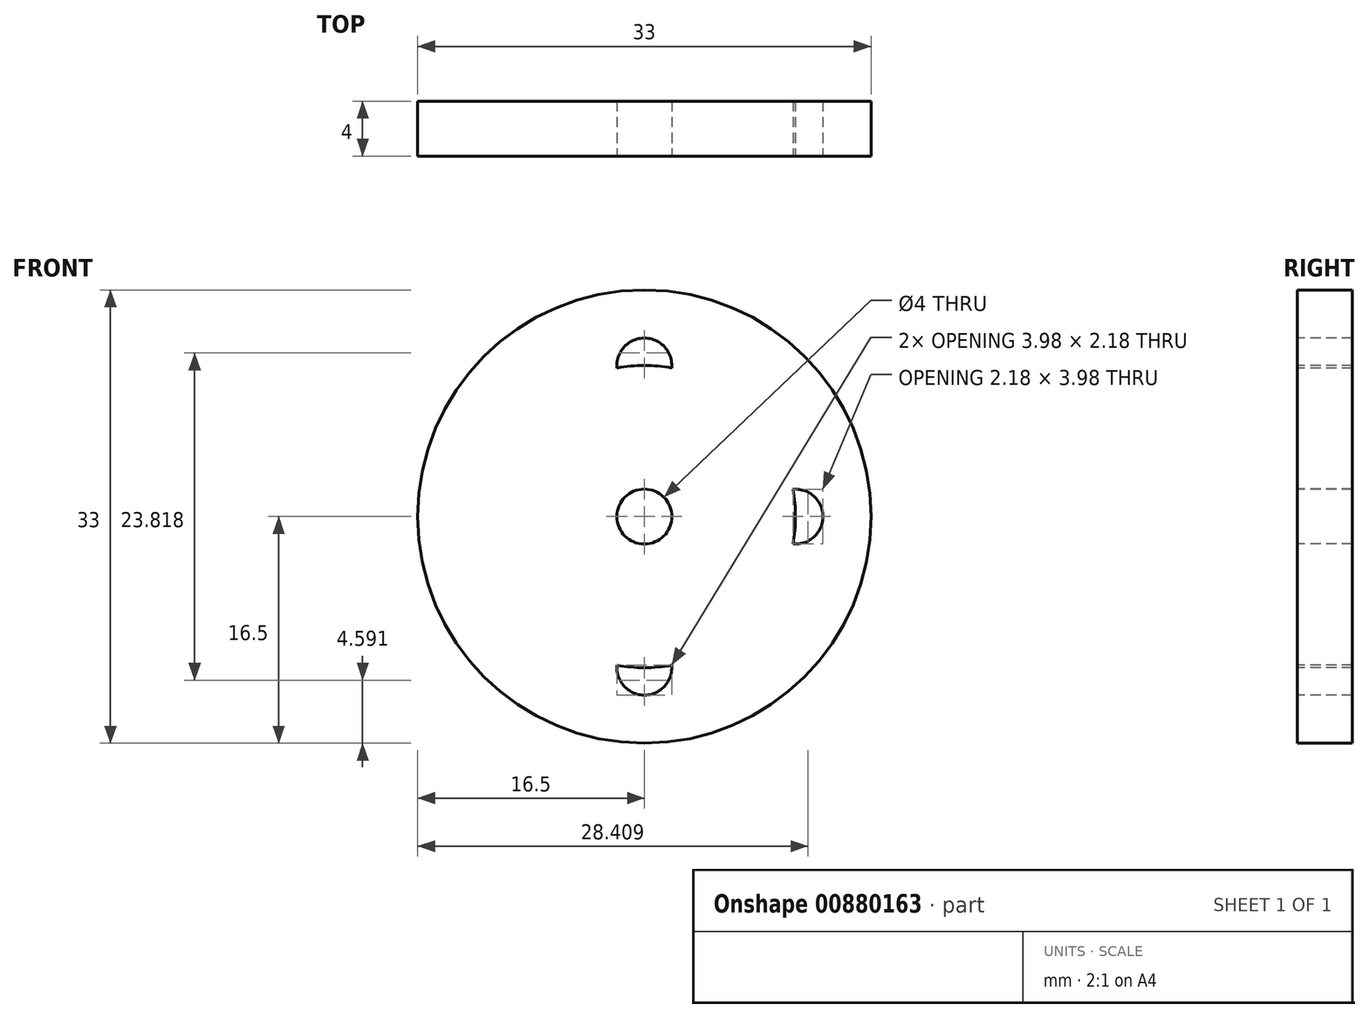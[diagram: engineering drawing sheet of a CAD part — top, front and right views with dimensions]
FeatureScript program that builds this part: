
annotation { "Feature Type Name" : "Feature", "Feature Type Description" : "" }
export const myFeature = defineFeature(function(context is Context, id is Id, definition is map)
    precondition{}
    {
        {
            var Q0;
            Q0=qCreatedBy(makeId("Front.planeOp"),FACE);
            var sketch = newSketch(context, id + "F0", { "sketchPlane" : qUnion([Q0])});
            skCircle(sketch, "E0", {"center": v(0, 0) * mm, "radius": 16.5 * mm});
            skSolve(sketch);
        }
        {
            var Q0;
            Q0 = qSketchRegion(id + "F0", true);
            extrude(context, id + "F1", {"entities" : qUnion([Q0]), "depth" : 4 * mm, "offsetDistance" : 25 * mm});
        }
        {
            var Q0;
            Q0=makeQuery(id+"F1.opExtrude","CAP_FACE",FACE,{"disambiguationData":[OSD([sQuery(id+"F0.wireOp",EDGE,"E0")])],"isStart":false});
            var sketch = newSketch(context, id + "F2", { "sketchPlane" : qUnion([Q0])});
            skLineSegment(sketch, "E1", {"start": v(0, 0) * mm, "end": v(-16.5, 0) * mm});
            skLineSegment(sketch, "E2", {"start": v(-16.5, 0) * mm, "end": v(0, 0) * mm});
            skLineSegment(sketch, "E3", {"start": v(0, 0) * mm, "end": v(0, 16.5) * mm});
            skLineSegment(sketch, "E4", {"start": v(0, 0) * mm, "end": v(0, -16.5) * mm});
            skLineSegment(sketch, "E5", {"start": v(0, 0) * mm, "end": v(16.5, 0) * mm});
            skLineSegment(sketch, "E6", {"start": v(16.5, 0) * mm, "end": v(9.5, 0) * mm});
            skLineSegment(sketch, "E7", {"start": v(-16.5, 0) * mm, "end": v(-9.5, 0) * mm});
            skLineSegment(sketch, "E8", {"start": v(0, -16.5) * mm, "end": v(0, -9.5) * mm});
            skLineSegment(sketch, "E9", {"start": v(0, 16.5) * mm, "end": v(0, 9.5) * mm});
            skCircle(sketch, "E10", {"center": v(0, 0) * mm, "radius": 2 * mm});
            skCircle(sketch, "E11", {"center": v(0, 0) * mm, "radius": 11 * mm});
            skCircle(sketch, "E12", {"center": v(0, 11) * mm, "radius": 2 * mm});
            skCircle(sketch, "E13", {"center": v(11, 0) * mm, "radius": 2 * mm});
            skCircle(sketch, "E14", {"center": v(0, -11) * mm, "radius": 2 * mm});
            skCircle(sketch, "E15", {"center": v(-11, 0) * mm, "radius": 2 * mm});
            skSolve(sketch);
        }
        {
            var Q0;
            {var subQ0=sQuery(id+"F2.wireOp",EDGE,"E7");var subQ1=sQuery(id+"F2.wireOp",EDGE,"E2");var subQ2=makeQuery(id+"F2.imprint","INTERSECT",VERTEX,{"derivedFrom":[subQ1,subQ0]});Q0=makeQuery(id+"F2.imprint","IMPRINT",FACE,{"disambiguationData":[TD([[makeQuery(id+"F2.imprint","IMPRINT",EDGE,{"disambiguationData":[TD([[subQ2,-1.0]])],"derivedFrom":subQ1}),1.0]])]});}
            var Q1;
            {var subQ0=sQuery(id+"F2.wireOp",EDGE,"E7");var subQ1=sQuery(id+"F2.wireOp",EDGE,"E2");var subQ2=makeQuery(id+"F2.imprint","INTERSECT",VERTEX,{"derivedFrom":[subQ1,subQ0]});Q1=makeQuery(id+"F2.imprint","IMPRINT",FACE,{"disambiguationData":[TD([[makeQuery(id+"F2.imprint","IMPRINT",EDGE,{"disambiguationData":[TD([[subQ2,-1.0]])],"derivedFrom":subQ1}),-1.0]])]});}
            var Q2;
            {var subQ0=sQuery(id+"F2.wireOp",EDGE,"E9");var subQ1=sQuery(id+"F2.wireOp",EDGE,"E3");var subQ2=makeQuery(id+"F2.imprint","INTERSECT",VERTEX,{"derivedFrom":[subQ1,subQ0]});Q2=makeQuery(id+"F2.imprint","IMPRINT",FACE,{"disambiguationData":[TD([[makeQuery(id+"F2.imprint","IMPRINT",EDGE,{"disambiguationData":[TD([[subQ2,1.0]])],"derivedFrom":subQ1}),-1.0]])]});}
            var Q3;
            {var subQ0=sQuery(id+"F2.wireOp",EDGE,"E9");var subQ1=sQuery(id+"F2.wireOp",EDGE,"E3");var subQ2=makeQuery(id+"F2.imprint","INTERSECT",VERTEX,{"derivedFrom":[subQ1,subQ0]});Q3=makeQuery(id+"F2.imprint","IMPRINT",FACE,{"disambiguationData":[TD([[makeQuery(id+"F2.imprint","IMPRINT",EDGE,{"disambiguationData":[TD([[subQ2,1.0]])],"derivedFrom":subQ1}),1.0]])]});}
            var Q4;
            {var subQ0=sQuery(id+"F2.wireOp",EDGE,"E8");var subQ1=sQuery(id+"F2.wireOp",EDGE,"E4");var subQ2=makeQuery(id+"F2.imprint","INTERSECT",VERTEX,{"derivedFrom":[subQ1,subQ0]});Q4=makeQuery(id+"F2.imprint","IMPRINT",FACE,{"disambiguationData":[TD([[makeQuery(id+"F2.imprint","IMPRINT",EDGE,{"disambiguationData":[TD([[subQ2,1.0]])],"derivedFrom":subQ1}),-1.0]])]});}
            var Q5;
            {var subQ0=sQuery(id+"F2.wireOp",EDGE,"E8");var subQ1=sQuery(id+"F2.wireOp",EDGE,"E4");var subQ2=makeQuery(id+"F2.imprint","INTERSECT",VERTEX,{"derivedFrom":[subQ1,subQ0]});Q5=makeQuery(id+"F2.imprint","IMPRINT",FACE,{"disambiguationData":[TD([[makeQuery(id+"F2.imprint","IMPRINT",EDGE,{"disambiguationData":[TD([[subQ2,1.0]])],"derivedFrom":subQ1}),1.0]])]});}
            var Q6;
            {var subQ0=sQuery(id+"F2.wireOp",EDGE,"E6");var subQ1=sQuery(id+"F2.wireOp",EDGE,"E5");var subQ2=makeQuery(id+"F2.imprint","INTERSECT",VERTEX,{"derivedFrom":[subQ1,subQ0]});Q6=makeQuery(id+"F2.imprint","IMPRINT",FACE,{"disambiguationData":[TD([[makeQuery(id+"F2.imprint","IMPRINT",EDGE,{"disambiguationData":[TD([[subQ2,1.0]])],"derivedFrom":subQ1}),1.0]])]});}
            var Q7;
            {var subQ0=sQuery(id+"F2.wireOp",EDGE,"E6");var subQ1=sQuery(id+"F2.wireOp",EDGE,"E5");var subQ2=makeQuery(id+"F2.imprint","INTERSECT",VERTEX,{"derivedFrom":[subQ1,subQ0]});Q7=makeQuery(id+"F2.imprint","IMPRINT",FACE,{"disambiguationData":[TD([[makeQuery(id+"F2.imprint","IMPRINT",EDGE,{"disambiguationData":[TD([[subQ2,1.0]])],"derivedFrom":subQ1}),-1.0]])]});}
            var Q8;
            {var subQ0=sQuery(id+"F2.wireOp",EDGE,"E13");var subQ1=sQuery(id+"F2.wireOp",EDGE,"E6");var subQ2=makeQuery(id+"F2.imprint","INTERSECT",VERTEX,{"derivedFrom":[subQ1,subQ0]});Q8=makeQuery(id+"F2.imprint","IMPRINT",FACE,{"disambiguationData":[TD([[makeQuery(id+"F2.imprint","IMPRINT",EDGE,{"disambiguationData":[TD([[subQ2,-1.0]])],"derivedFrom":subQ1}),-1.0]])]});}
            var Q9;
            {var subQ0=sQuery(id+"F2.wireOp",EDGE,"E13");var subQ1=sQuery(id+"F2.wireOp",EDGE,"E6");var subQ2=makeQuery(id+"F2.imprint","INTERSECT",VERTEX,{"derivedFrom":[subQ1,subQ0]});Q9=makeQuery(id+"F2.imprint","IMPRINT",FACE,{"disambiguationData":[TD([[makeQuery(id+"F2.imprint","IMPRINT",EDGE,{"disambiguationData":[TD([[subQ2,-1.0]])],"derivedFrom":subQ1}),1.0]])]});}
            var Q10;
            {var subQ0=sQuery(id+"F2.wireOp",EDGE,"E15");var subQ1=sQuery(id+"F2.wireOp",EDGE,"E7");var subQ2=makeQuery(id+"F2.imprint","INTERSECT",VERTEX,{"derivedFrom":[subQ1,subQ0]});Q10=makeQuery(id+"F2.imprint","IMPRINT",FACE,{"disambiguationData":[TD([[makeQuery(id+"F2.imprint","IMPRINT",EDGE,{"disambiguationData":[TD([[subQ2,-1.0]])],"derivedFrom":subQ1}),1.0]])]});}
            var Q11;
            {var subQ0=sQuery(id+"F2.wireOp",EDGE,"E15");var subQ1=sQuery(id+"F2.wireOp",EDGE,"E7");var subQ2=makeQuery(id+"F2.imprint","INTERSECT",VERTEX,{"derivedFrom":[subQ1,subQ0]});Q11=makeQuery(id+"F2.imprint","IMPRINT",FACE,{"disambiguationData":[TD([[makeQuery(id+"F2.imprint","IMPRINT",EDGE,{"disambiguationData":[TD([[subQ2,-1.0]])],"derivedFrom":subQ1}),-1.0]])]});}
            var Q12;
            {var subQ0=sQuery(id+"F2.wireOp",EDGE,"E14");var subQ1=sQuery(id+"F2.wireOp",EDGE,"E8");var subQ2=makeQuery(id+"F2.imprint","INTERSECT",VERTEX,{"derivedFrom":[subQ1,subQ0]});Q12=makeQuery(id+"F2.imprint","IMPRINT",FACE,{"disambiguationData":[TD([[makeQuery(id+"F2.imprint","IMPRINT",EDGE,{"disambiguationData":[TD([[subQ2,-1.0]])],"derivedFrom":subQ1}),1.0]])]});}
            var Q13;
            {var subQ0=sQuery(id+"F2.wireOp",EDGE,"E14");var subQ1=sQuery(id+"F2.wireOp",EDGE,"E8");var subQ2=makeQuery(id+"F2.imprint","INTERSECT",VERTEX,{"derivedFrom":[subQ1,subQ0]});Q13=makeQuery(id+"F2.imprint","IMPRINT",FACE,{"disambiguationData":[TD([[makeQuery(id+"F2.imprint","IMPRINT",EDGE,{"disambiguationData":[TD([[subQ2,-1.0]])],"derivedFrom":subQ1}),-1.0]])]});}
            var Q14;
            {var subQ0=sQuery(id+"F2.wireOp",EDGE,"E12");var subQ1=sQuery(id+"F2.wireOp",EDGE,"E9");var subQ2=makeQuery(id+"F2.imprint","INTERSECT",VERTEX,{"derivedFrom":[subQ1,subQ0]});Q14=makeQuery(id+"F2.imprint","IMPRINT",FACE,{"disambiguationData":[TD([[makeQuery(id+"F2.imprint","IMPRINT",EDGE,{"disambiguationData":[TD([[subQ2,-1.0]])],"derivedFrom":subQ1}),1.0]])]});}
            var Q15;
            {var subQ0=sQuery(id+"F2.wireOp",EDGE,"E12");var subQ1=sQuery(id+"F2.wireOp",EDGE,"E9");var subQ2=makeQuery(id+"F2.imprint","INTERSECT",VERTEX,{"derivedFrom":[subQ1,subQ0]});Q15=makeQuery(id+"F2.imprint","IMPRINT",FACE,{"disambiguationData":[TD([[makeQuery(id+"F2.imprint","IMPRINT",EDGE,{"disambiguationData":[TD([[subQ2,-1.0]])],"derivedFrom":subQ1}),-1.0]])]});}
            var Q16;
            {var subQ1=sQuery(id+"F2.wireOp",EDGE,"E2");var subQ3=sQuery(id+"F2.wireOp",EDGE,"E10");var subQ4=makeQuery(id+"F2.imprint","INTERSECT",VERTEX,{"derivedFrom":[subQ1,subQ3]});Q16=makeQuery(id+"F2.imprint","IMPRINT",FACE,{"disambiguationData":[TD([[makeQuery(id+"F2.imprint","IMPRINT",EDGE,{"disambiguationData":[TD([[subQ4,1.0]])],"derivedFrom":subQ3}),1.0]])]});}
            var Q17;
            {var subQ1=sQuery(id+"F2.wireOp",EDGE,"E3");var subQ3=sQuery(id+"F2.wireOp",EDGE,"E10");var subQ4=makeQuery(id+"F2.imprint","INTERSECT",VERTEX,{"derivedFrom":[subQ1,subQ3]});Q17=makeQuery(id+"F2.imprint","IMPRINT",FACE,{"disambiguationData":[TD([[makeQuery(id+"F2.imprint","IMPRINT",EDGE,{"disambiguationData":[TD([[subQ4,1.0]])],"derivedFrom":subQ3}),1.0]])]});}
            var Q18;
            {var subQ1=sQuery(id+"F2.wireOp",EDGE,"E4");var subQ3=sQuery(id+"F2.wireOp",EDGE,"E10");var subQ4=makeQuery(id+"F2.imprint","INTERSECT",VERTEX,{"derivedFrom":[subQ1,subQ3]});Q18=makeQuery(id+"F2.imprint","IMPRINT",FACE,{"disambiguationData":[TD([[makeQuery(id+"F2.imprint","IMPRINT",EDGE,{"disambiguationData":[TD([[subQ4,-1.0]])],"derivedFrom":subQ3}),1.0]])]});}
            var Q19;
            {var subQ1=sQuery(id+"F2.wireOp",EDGE,"E2");var subQ3=sQuery(id+"F2.wireOp",EDGE,"E10");var subQ4=makeQuery(id+"F2.imprint","INTERSECT",VERTEX,{"derivedFrom":[subQ1,subQ3]});Q19=makeQuery(id+"F2.imprint","IMPRINT",FACE,{"disambiguationData":[TD([[makeQuery(id+"F2.imprint","IMPRINT",EDGE,{"disambiguationData":[TD([[subQ4,-1.0]])],"derivedFrom":subQ3}),1.0]])]});}
            extrude(context, id + "F3", {"entities" : qUnion([Q0, Q1, Q2, Q3, Q4, Q5, Q6, Q7, Q8, Q9, Q10, Q11, Q12, Q13, Q14, Q15, Q16, Q17, Q18, Q19]), "operationType" : NewBodyOperationType.REMOVE, "endBound" : BoundingType.THROUGH_ALL, "oppositeDirection" : true, "depth" : 25 * mm, "offsetDistance" : 25 * mm});
        }
    });
